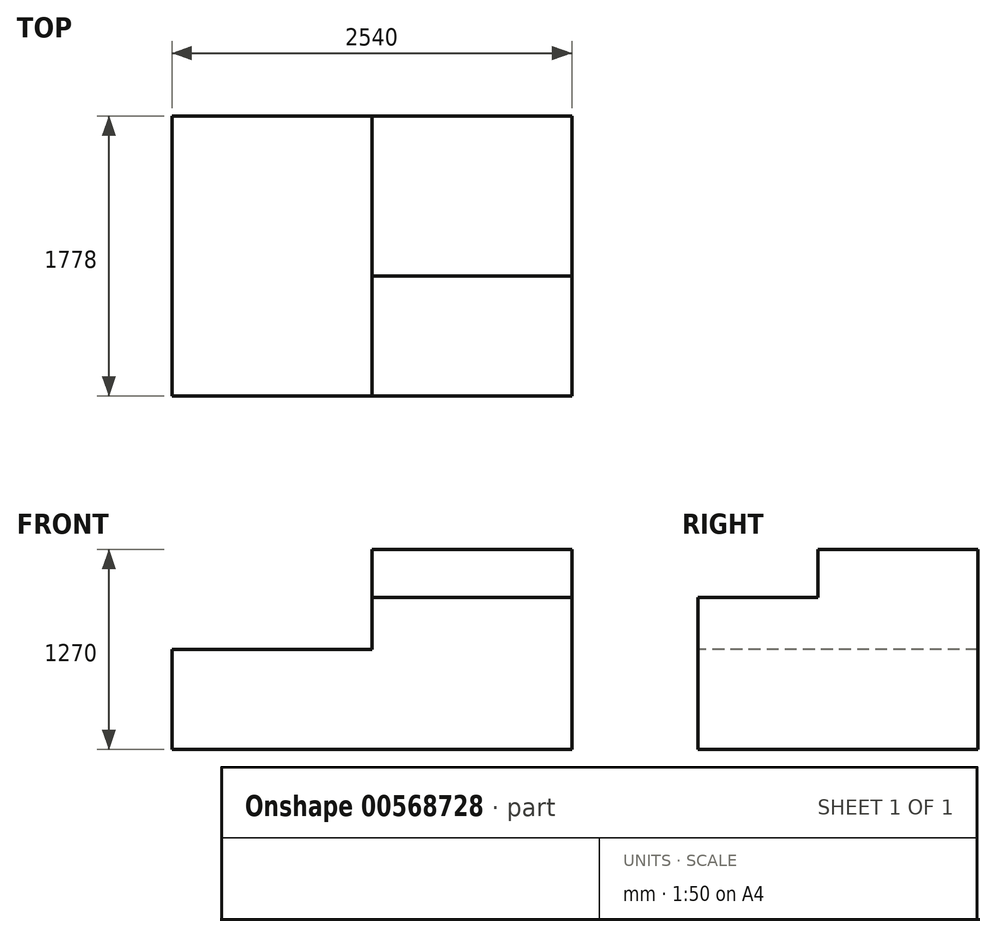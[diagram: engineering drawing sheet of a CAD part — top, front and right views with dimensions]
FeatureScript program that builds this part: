
annotation { "Feature Type Name" : "Feature", "Feature Type Description" : "" }
export const myFeature = defineFeature(function(context is Context, id is Id, definition is map)
    precondition{}
    {
        {
            var Q0;
            Q0=qCreatedBy(makeId("Front.planeOp"),FACE);
            var sketch = newSketch(context, id + "F0", { "sketchPlane" : qUnion([Q0])});
            skLineSegment(sketch, "E0.bottom", {"start": v(0, 0) * mm, "end": v(2540, 0) * mm});
            skLineSegment(sketch, "E0.top", {"start": v(0, 1270) * mm, "end": v(2540, 1270) * mm});
            skLineSegment(sketch, "E0.left", {"start": v(0, 0) * mm, "end": v(0, 1270) * mm});
            skLineSegment(sketch, "E0.right", {"start": v(2540, 0) * mm, "end": v(2540, 1270) * mm});
            skSolve(sketch);
        }
        {
            var Q0;
            Q0=makeQuery(id+"F0.imprint","IMPRINT",FACE,{"disambiguationData":[TD([[makeQuery(id+"F0.imprint","IMPRINT",EDGE,{"derivedFrom":sQuery(id+"F0.wireOp",EDGE,"E0.bottom")}),1.0]])]});
            extrude(context, id + "F1", {"entities" : qUnion([Q0]), "depth" : 1778 * mm, "offsetDistance" : 25.4 * mm});
        }
        {
            var Q0;
            Q0=makeQuery(id+"F1.opExtrude","CAP_FACE",FACE,{"disambiguationData":[OSD([sQuery(id+"F0.wireOp",EDGE,"E0.bottom"),sQuery(id+"F0.wireOp",EDGE,"E0.top"),sQuery(id+"F0.wireOp",EDGE,"E0.left"),sQuery(id+"F0.wireOp",EDGE,"E0.right")])],"isStart":false});
            var sketch = newSketch(context, id + "F2", { "sketchPlane" : qUnion([Q0])});
            skLineSegment(sketch, "E1.bottom", {"start": v(0, 1270) * mm, "end": v(1270, 1270) * mm});
            skLineSegment(sketch, "E1.top", {"start": v(0, 635) * mm, "end": v(1270, 635) * mm});
            skLineSegment(sketch, "E1.left", {"start": v(0, 1270) * mm, "end": v(0, 635) * mm});
            skLineSegment(sketch, "E1.right", {"start": v(1270, 1270) * mm, "end": v(1270, 635) * mm});
            skSolve(sketch);
        }
        {
            var Q0;
            Q0=makeQuery(id+"F2.imprint","IMPRINT",FACE,{"disambiguationData":[TD([[makeQuery(id+"F2.imprint","IMPRINT",EDGE,{"derivedFrom":sQuery(id+"F2.wireOp",EDGE,"E1.bottom")}),-1.0]])]});
            extrude(context, id + "F3", {"entities" : qUnion([Q0]), "operationType" : NewBodyOperationType.REMOVE, "endBound" : BoundingType.THROUGH_ALL, "oppositeDirection" : true, "depth" : 25.4 * mm, "offsetDistance" : 25.4 * mm});
        }
        {
            var Q0;
            Q0=makeQuery(id+"F1.opExtrude","CAP_FACE",FACE,{"disambiguationData":[OSD([sQuery(id+"F0.wireOp",EDGE,"E0.bottom"),sQuery(id+"F0.wireOp",EDGE,"E0.top"),sQuery(id+"F0.wireOp",EDGE,"E0.left"),sQuery(id+"F0.wireOp",EDGE,"E0.right")])],"isStart":false});
            var sketch = newSketch(context, id + "F4", { "sketchPlane" : qUnion([Q0])});
            skLineSegment(sketch, "E2.bottom", {"start": v(1270, 1270) * mm, "end": v(2540, 1270) * mm});
            skLineSegment(sketch, "E2.top", {"start": v(1270, 965.2) * mm, "end": v(2540, 965.2) * mm});
            skLineSegment(sketch, "E2.left", {"start": v(1270, 1270) * mm, "end": v(1270, 965.2) * mm});
            skLineSegment(sketch, "E2.right", {"start": v(2540, 1270) * mm, "end": v(2540, 965.2) * mm});
            skSolve(sketch);
        }
        {
            var Q0;
            Q0=makeQuery(id+"F4.imprint","IMPRINT",FACE,{"disambiguationData":[TD([[makeQuery(id+"F4.imprint","IMPRINT",EDGE,{"derivedFrom":sQuery(id+"F4.wireOp",EDGE,"E2.bottom")}),-1.0]])]});
            extrude(context, id + "F5", {"entities" : qUnion([Q0]), "operationType" : NewBodyOperationType.REMOVE, "oppositeDirection" : true, "depth" : 762 * mm, "offsetDistance" : 25.4 * mm});
        }
    });
